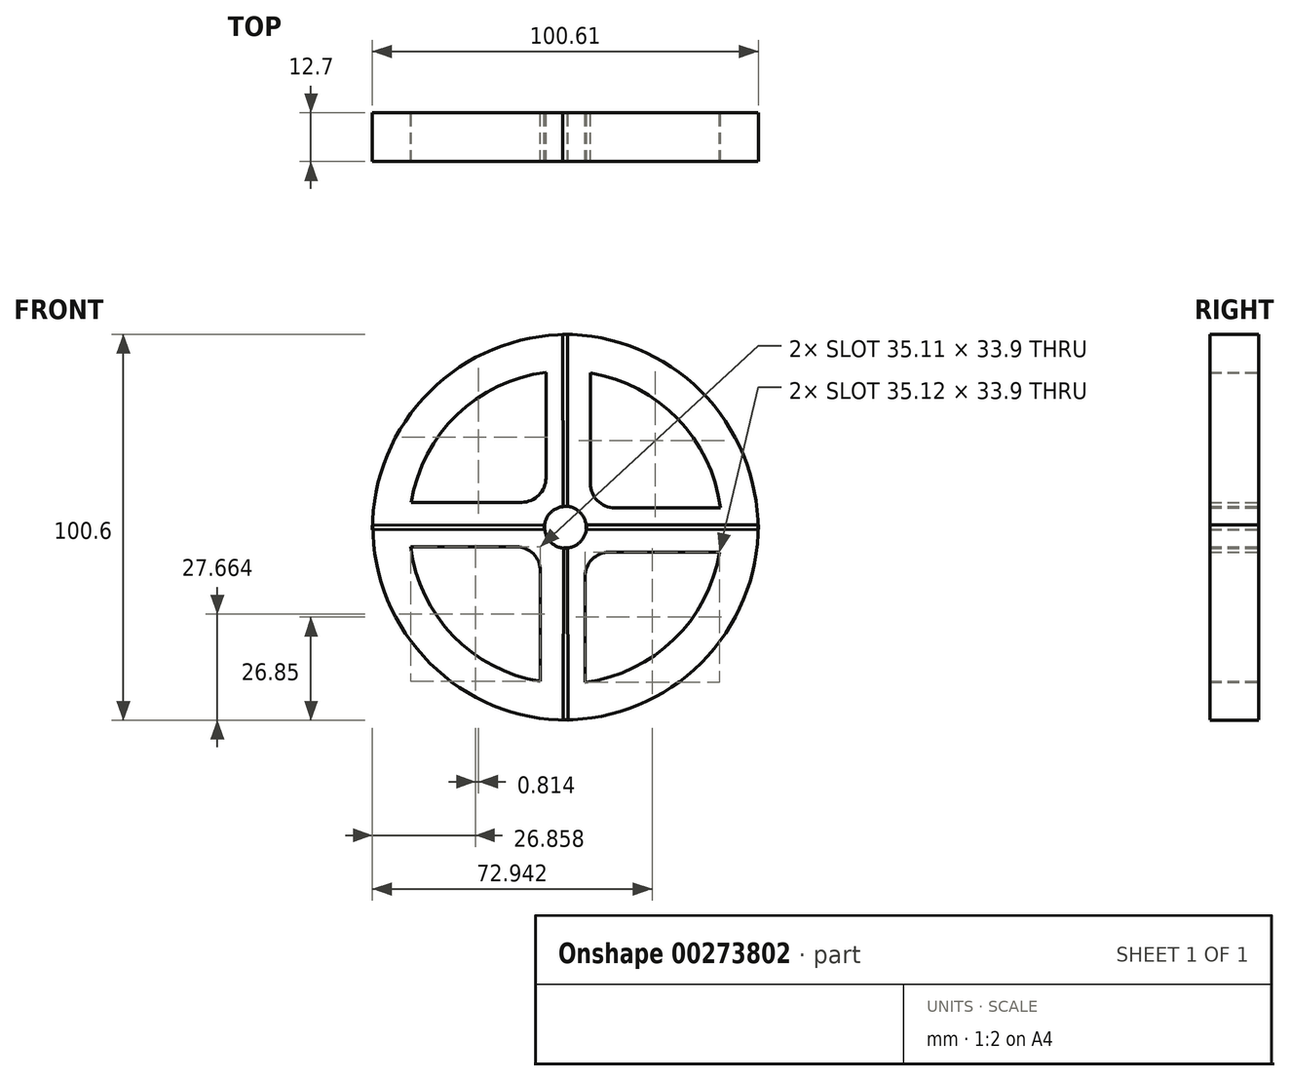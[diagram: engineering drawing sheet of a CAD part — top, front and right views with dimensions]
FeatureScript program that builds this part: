
annotation { "Feature Type Name" : "Feature", "Feature Type Description" : "" }
export const myFeature = defineFeature(function(context is Context, id is Id, definition is map)
    precondition{}
    {
        {
            var Q0;
            Q0=qCreatedBy(makeId("Front.planeOp"),FACE);
            var sketch = newSketch(context, id + "F0", { "sketchPlane" : qUnion([Q0])});
            skArc(sketch, "E0", {"start": v(50.3, -0.6) * mm, "mid": v(35.41, 35.41) * mm, "end": v(-0.6, 50.3) * mm});
            skLineSegment(sketch, "E1", {"start": v(-0.6, 50.3) * mm, "end": v(-0.5, -0.5) * mm});
            skLineSegment(sketch, "E2", {"start": v(-0.5, -0.5) * mm, "end": v(50.3, -0.6) * mm});
            skSolve(sketch);
        }
        {
            var Q0;
            Q0=qCreatedBy(makeId("Front.planeOp"),FACE);
            var sketch = newSketch(context, id + "F1", { "sketchPlane" : qUnion([Q0])});
            skArc(sketch, "E3", {"start": v(40.46, 5.07) * mm, "mid": v(29.36, 28.27) * mm, "end": v(6.57, 40.18) * mm});
            skLineSegment(sketch, "E4", {"start": v(6.57, 40.18) * mm, "end": v(6.57, 11.42) * mm});
            skLineSegment(sketch, "E5", {"start": v(12.92, 5.07) * mm, "end": v(40.46, 5.07) * mm});
            skPoint(sketch, "E6.visualSharp", {"position": v(6.57, 5.07) * mm});
            skArc(sketch, "E6.filletArc", {"start": v(6.57, 11.42) * mm, "mid": v(8.43, 6.93) * mm, "end": v(12.92, 5.07) * mm});
            skSolve(sketch);
        }
        {
            var Q0;
            Q0=makeQuery(id+"F0.imprint","IMPRINT",FACE,{"disambiguationData":[TD([[makeQuery(id+"F0.imprint","IMPRINT",EDGE,{"derivedFrom":sQuery(id+"F0.wireOp",EDGE,"E0")}),1.0]])]});
            extrude(context, id + "F2", {"entities" : qUnion([Q0]), "depth" : 12.7 * mm});
        }
        {
            var Q0;
            Q0 = qSketchRegion(id + "F1", true);
            extrude(context, id + "F3", {"entities" : qUnion([Q0]), "operationType" : NewBodyOperationType.REMOVE, "depth" : 25.4 * mm});
        }
        {
            var Q0;
            Q0=qCreatedBy(makeId("Front.planeOp"),FACE);
            var sketch = newSketch(context, id + "F4", { "sketchPlane" : qUnion([Q0])});
            skArc(sketch, "E7", {"start": v(5.46, -0.53) * mm, "mid": v(3.84, 3.9) * mm, "end": v(-0.62, 5.45) * mm});
            skLineSegment(sketch, "E8", {"start": v(-0.62, 5.45) * mm, "end": v(-0.62, -0.53) * mm});
            skLineSegment(sketch, "E9", {"start": v(-0.62, -0.53) * mm, "end": v(5.46, -0.53) * mm});
            skSolve(sketch);
        }
        {
            var Q0;
            Q0 = qSketchRegion(id + "F4", true);
            extrude(context, id + "F5", {"entities" : qUnion([Q0]), "operationType" : NewBodyOperationType.REMOVE, "depth" : 25.4 * mm});
        }
        {
            var Q0;
            Q0=makeQuery(id+"F2.opExtrude","SWEPT_BODY",BODY,{"disambiguationData":[OSD([sQuery(id+"F0.wireOp",EDGE,"E0"),sQuery(id+"F0.wireOp",EDGE,"E1"),sQuery(id+"F0.wireOp",EDGE,"E2")])]});
            var Q1;
            Q1=makeQuery(id+"F3.boolean.opBoolean","COPY",FACE,{"derivedFrom":makeQuery(id+"F3.opExtrude","SWEPT_FACE",FACE,{"disambiguationData":[OSD([sQuery(id+"F1.wireOp",EDGE,"E3")])]})});
            circularPattern(context, id + "F6", {"entities" : qUnion([Q0]), "axis" : qUnion([Q1]), "angle" : 360 * degree, "instanceCount" : 4, "equalSpace" : true});
        }
        {
            var Q0;
            Q0=qCreatedBy(makeId("Front.planeOp"),FACE);
            cPlane(context, id + "F7", {"entities" : qUnion([Q0]), "cplaneType" : CPlaneType.OFFSET, "offset" : 101.6 * mm, "width" : 152.4 * mm, "height" : 152.4 * mm});
        }
    });
